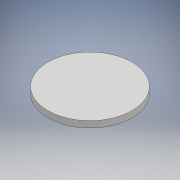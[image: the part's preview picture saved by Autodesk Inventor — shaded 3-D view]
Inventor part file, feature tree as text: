
AUTODESK INVENTOR PART (.ipt)
format: ipt  version: 2018 (Build 220112000, 112)  size: 90,112 bytes
history: native  units: mm
features: other x1, extrude x1, sketch x1
ambient origin geometry x8: Origin, YZ Plane, XZ Plane, XY Plane, X Axis, Y Axis, Z Axis, Center Point
bodies: Body1 (feature_tree)
feature tree (3):
  other  "Bryła1"
  extrude  "Wyciągnięcie proste1"  Depth=80.0mm
  sketch  "Szkic1"
